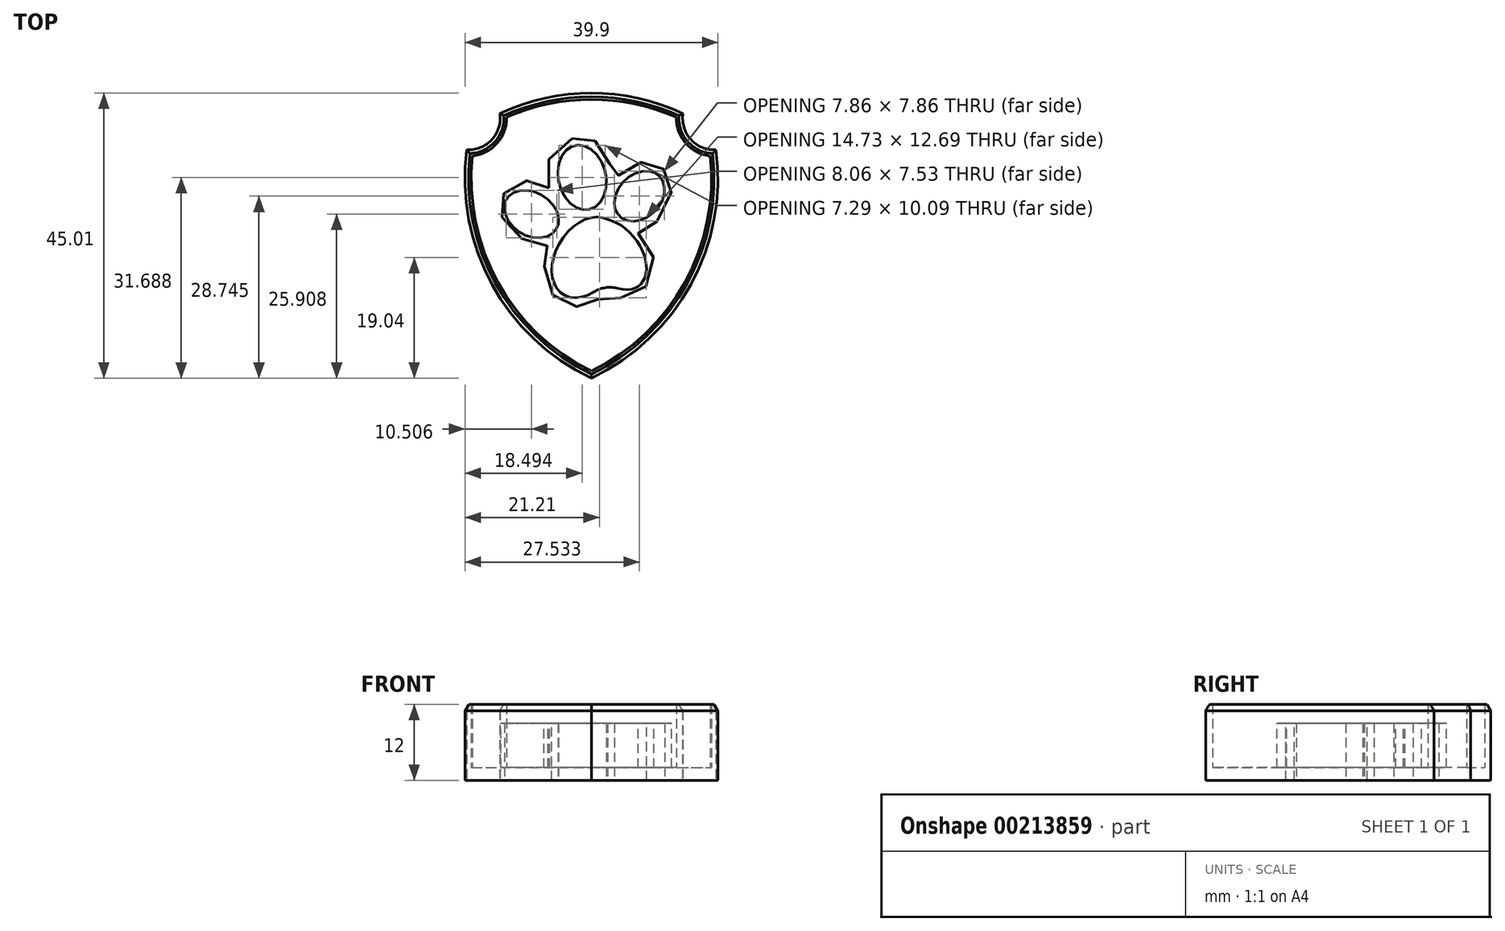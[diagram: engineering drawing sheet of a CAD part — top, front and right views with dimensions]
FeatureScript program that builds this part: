
annotation { "Feature Type Name" : "Feature", "Feature Type Description" : "" }
export const myFeature = defineFeature(function(context is Context, id is Id, definition is map)
    precondition{}
    {
        {
            var Q0;
            Q0=qCreatedBy(makeId("Top.planeOp"),FACE);
            var sketch = newSketch(context, id + "F0", { "sketchPlane" : qUnion([Q0])});
            skLineSegment(sketch, "E0", {"start": v(0, 25) * mm, "end": v(0, -25) * mm, "construction": true});
            skArc(sketch, "E1", {"start": v(-14.44, 19.95) * mm, "mid": v(0, 23.16) * mm, "end": v(14.44, 19.95) * mm});
            skArc(sketch, "E2", {"start": v(-14.44, 19.95) * mm, "mid": v(-15.68, 15.84) * mm, "end": v(-19.65, 14.2) * mm});
            skArc(sketch, "E3", {"start": v(14.44, 19.95) * mm, "mid": v(15.68, 15.84) * mm, "end": v(19.65, 14.2) * mm});
            skArc(sketch, "E4", {"start": v(0, -21.85) * mm, "mid": v(-15.7, -7.03) * mm, "end": v(-19.65, 14.2) * mm});
            skArc(sketch, "E5", {"start": v(19.65, 14.2) * mm, "mid": v(15.7, -7.03) * mm, "end": v(0, -21.85) * mm});
            skSolve(sketch);
        }
        {
            var Q0;
            Q0 = qSketchRegion(id + "F0", true);
            extrude(context, id + "F1", {"entities" : qUnion([Q0]), "depth" : 2 * mm});
        }
        {
            var Q0;
            Q0=qCreatedBy(makeId("Top.planeOp"),FACE);
            var sketch = newSketch(context, id + "F2", { "sketchPlane" : qUnion([Q0])});
            skArc(sketch, "E6.0", {"start": v(-14.44, 19.95) * mm, "mid": v(0, 23.16) * mm, "end": v(14.44, 19.95) * mm});
            skArc(sketch, "E6.1", {"start": v(-14.44, 19.95) * mm, "mid": v(-15.68, 15.84) * mm, "end": v(-19.65, 14.2) * mm});
            skArc(sketch, "E6.2", {"start": v(0, -21.85) * mm, "mid": v(-15.7, -7.03) * mm, "end": v(-19.65, 14.2) * mm});
            skArc(sketch, "E6.3", {"start": v(14.44, 19.95) * mm, "mid": v(15.68, 15.84) * mm, "end": v(19.65, 14.2) * mm});
            skArc(sketch, "E7.0", {"start": v(-13.39, 19.33) * mm, "mid": v(-14.89, 15.23) * mm, "end": v(-18.76, 13.22) * mm});
            skArc(sketch, "E7.1", {"start": v(0, -20.74) * mm, "mid": v(-14.73, -6.71) * mm, "end": v(-18.76, 13.22) * mm});
            skArc(sketch, "E7.2", {"start": v(-13.39, 19.33) * mm, "mid": v(0, 22.16) * mm, "end": v(13.39, 19.33) * mm});
            skArc(sketch, "E7.3", {"start": v(13.39, 19.33) * mm, "mid": v(14.89, 15.23) * mm, "end": v(18.76, 13.22) * mm});
            skArc(sketch, "E7.4", {"start": v(18.76, 13.22) * mm, "mid": v(14.73, -6.71) * mm, "end": v(0, -20.74) * mm});
            skArc(sketch, "E8.0", {"start": v(19.65, 14.2) * mm, "mid": v(15.7, -7.03) * mm, "end": v(0, -21.85) * mm});
            skSolve(sketch);
        }
        {
            var Q0;
            Q0 = qSketchRegion(id + "F2", true);
            extrude(context, id + "F3", {"entities" : qUnion([Q0]), "operationType" : NewBodyOperationType.ADD, "depth" : 12 * mm});
        }
        {
            var Q0;
            Q0=qCreatedBy(makeId("Top.planeOp"),FACE);
            var sketch = newSketch(context, id + "F4", { "sketchPlane" : qUnion([Q0])});
            skEllipse(sketch, "E9", {"center": v(-9.44, 4.06) * mm, "majorRadius": 4.58 * mm, "minorRadius": 3.42 * mm, "majorAxis": v(0.85, -0.53)});
            skEllipse(sketch, "E10", {"center": v(-1.46, 9.84) * mm, "majorRadius": 5.18 * mm, "minorRadius": 3.74 * mm, "majorAxis": v(0.22, -0.97)});
            skEllipse(sketch, "E11", {"center": v(7.58, 6.9) * mm, "majorRadius": 4.46 * mm, "minorRadius": 3.4 * mm, "majorAxis": v(0.7, 0.7)});
            skEllipticalArc(sketch, "E12", {});
            skEllipticalArc(sketch, "E13", {});
            skPoint(sketch, "E14.visualSharp", {"position": v(2.19, -6.69) * mm});
            skArc(sketch, "E14.filletArc", {"start": v(4.29, -7.69) * mm, "mid": v(2.25, -7.56) * mm, "end": v(0.34, -8.26) * mm});
            const initialGuessF4  = {"E12": [-0.000825658324174583, -0.0027743864338845015, 0.5189781024771581, 0.8547875345073818, 0.006885848797741289, 0.004767301582334577, 0.046636328894096385, 4.077954499657045], "E13": [0.0034836893901228905, -0.0022488562390208244, 0.6385724586285335, -0.7695617032318526, 0.006419216435122319, 0.004185572444733501, 5.533444123706438, 2.4160858860053582]};
            skSetInitialGuess(sketch, initialGuessF4);
            skSolve(sketch);
        }
        {
            var Q0;
            Q0=qCreatedBy(makeId("Top.planeOp"),FACE);
            var sketch = newSketch(context, id + "F5", { "sketchPlane" : qUnion([Q0])});
            skFitSpline(sketch, "E15", {"points": [v(-6.71, 8.16) * mm, v(-9.02, 9.2) * mm, v(-13.12, 8.16) * mm, v(-14.28, 5.63) * mm, v(-13.33, 2.06) * mm, v(-9.02, -0.57) * mm, v(-6.71, -1.2) * mm, v(-7.34, -3.83) * mm, v(-6.3, -8.45) * mm, v(-2.82, -10.55) * mm, v(-0.09, -9.92) * mm, v(2.43, -9.08) * mm, v(5.7, -9.08) * mm, v(9.26, -6.35) * mm, v(9.26, -1.4) * mm, v(7.37, 1.32) * mm, v(10.32, 2.9) * mm, v(12.63, 7.95) * mm, v(11.58, 11) * mm, v(8.84, 12.15) * mm, v(5.59, 11.52) * mm, v(3.48, 9.63) * mm, v(2.43, 13.73) * mm, v(0.02, 15.83) * mm, v(-2.82, 16.04) * mm, v(-6.71, 12.57) * mm, v(-6.71, 8.16) * mm]});
            skSolve(sketch);
        }
        {
            var Q0;
            Q0 = qSketchRegion(id + "F5", true);
            extrude(context, id + "F6", {"entities" : qUnion([Q0]), "operationType" : NewBodyOperationType.ADD, "depth" : 9 * mm});
        }
        {
            var Q0;
            Q0 = qSketchRegion(id + "F4", true);
            extrude(context, id + "F7", {"entities" : qUnion([Q0]), "operationType" : NewBodyOperationType.REMOVE, "endBound" : BoundingType.THROUGH_ALL, "depth" : 25 * mm});
        }
        {
            var Q0;
            Q0=makeQuery(id+"F3.opExtrude","CAP_EDGE",EDGE,{"disambiguationData":[OSD([sQuery(id+"F2.wireOp",EDGE,"E6.2")])],"isStart":false});
            var Q1;
            Q1=makeQuery(id+"F3.opExtrude","CAP_EDGE",EDGE,{"disambiguationData":[OSD([sQuery(id+"F2.wireOp",EDGE,"E6.1")])],"isStart":false});
            var Q2;
            Q2=makeQuery(id+"F3.opExtrude","CAP_EDGE",EDGE,{"disambiguationData":[OSD([sQuery(id+"F2.wireOp",EDGE,"E6.0")])],"isStart":false});
            var Q3;
            Q3=makeQuery(id+"F3.opExtrude","CAP_EDGE",EDGE,{"disambiguationData":[OSD([sQuery(id+"F2.wireOp",EDGE,"E6.3")])],"isStart":false});
            var Q4;
            Q4=makeQuery(id+"F3.opExtrude","CAP_EDGE",EDGE,{"disambiguationData":[OSD([sQuery(id+"F2.wireOp",EDGE,"E8.0")])],"isStart":false});
            chamfer(context, id + "F8", {"entities" : qUnion([Q0, Q1, Q2, Q3, Q4]), "chamferType" : ChamferType.OFFSET_ANGLE, "width" : 1 * mm, "oppositeDirection" : false, "angle" : 30 * degree, "tangentPropagation" : true});
        }
    });
